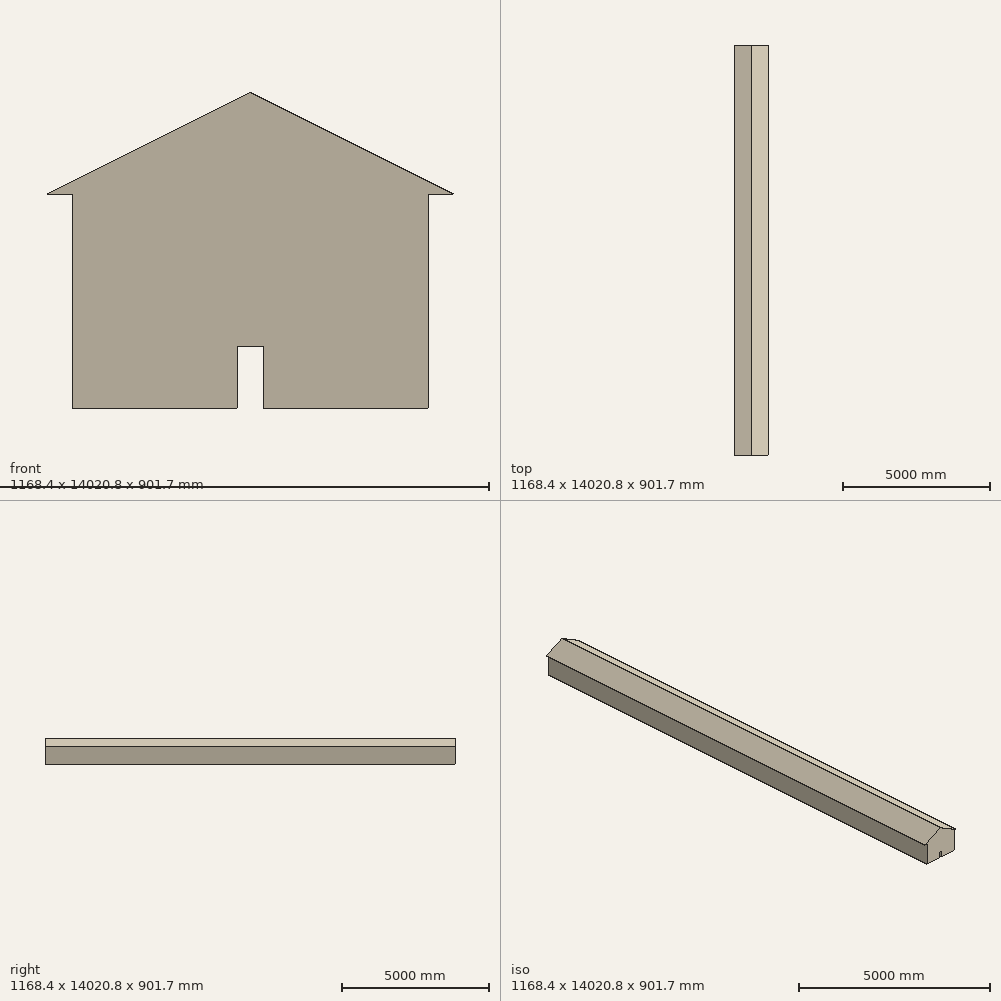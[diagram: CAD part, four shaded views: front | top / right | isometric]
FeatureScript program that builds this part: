
annotation { "Feature Type Name" : "Feature", "Feature Type Description" : "" }
export const myFeature = defineFeature(function(context is Context, id is Id, definition is map)
    precondition{}
    {
        {
            var Q0;
            Q0=qCreatedBy(makeId("Front.planeOp"),FACE);
            var sketch = newSketch(context, id + "F0", { "sketchPlane" : qUnion([Q0])});
            skLineSegment(sketch, "E0", {"start": v(0, 0) * mm, "end": v(-508, 0) * mm});
            skLineSegment(sketch, "E1", {"start": v(0, 0) * mm, "end": v(508, 0) * mm});
            skLineSegment(sketch, "E2", {"start": v(0, 254) * mm, "end": v(0, 0) * mm});
            skLineSegment(sketch, "E3", {"start": v(-508, 0) * mm, "end": v(0, 254) * mm});
            skLineSegment(sketch, "E4", {"start": v(-508, 0) * mm, "end": v(-584.2, 0) * mm});
            skLineSegment(sketch, "E5", {"start": v(508, 0) * mm, "end": v(584.2, 0) * mm});
            skLineSegment(sketch, "E6", {"start": v(0, 254) * mm, "end": v(0, 292.1) * mm});
            skLineSegment(sketch, "E7", {"start": v(-584.2, 0) * mm, "end": v(0, 292.1) * mm});
            skLineSegment(sketch, "E8", {"start": v(-508, 0) * mm, "end": v(-508, -609.6) * mm});
            skLineSegment(sketch, "E9", {"start": v(-508, -609.6) * mm, "end": v(508, -609.6) * mm});
            skLineSegment(sketch, "E10", {"start": v(0, 254) * mm, "end": v(508, 0) * mm});
            skLineSegment(sketch, "E11", {"start": v(0, 292.1) * mm, "end": v(584.2, 0) * mm});
            skLineSegment(sketch, "E12", {"start": v(508, 0) * mm, "end": v(508, -609.6) * mm});
            skLineSegment(sketch, "E13", {"start": v(0, -609.6) * mm, "end": v(-38.1, -609.6) * mm});
            skLineSegment(sketch, "E14", {"start": v(0, -609.6) * mm, "end": v(38.1, -609.6) * mm});
            skLineSegment(sketch, "E15", {"start": v(38.1, -609.6) * mm, "end": v(38.1, -431.8) * mm});
            skLineSegment(sketch, "E16", {"start": v(38.1, -431.8) * mm, "end": v(-38.1, -431.8) * mm});
            skLineSegment(sketch, "E17", {"start": v(-38.1, -431.8) * mm, "end": v(-38.1, -609.6) * mm});
            skLineSegment(sketch, "E18", {"start": v(-508, -609.6) * mm, "end": v(-508, -635) * mm});
            skLineSegment(sketch, "E19", {"start": v(-508, -635) * mm, "end": v(508, -635) * mm});
            skLineSegment(sketch, "E20", {"start": v(508, -635) * mm, "end": v(508, -609.6) * mm});
            skSolve(sketch);
        }
        {
            var Q0;
            Q0=makeQuery(id+"F0.imprint","IMPRINT",FACE,{"disambiguationData":[TD([[makeQuery(id+"F0.imprint","IMPRINT",EDGE,{"derivedFrom":sQuery(id+"F0.wireOp",EDGE,"E0")}),-1.0]])]});
            var Q1;
            Q1=makeQuery(id+"F0.imprint","IMPRINT",FACE,{"disambiguationData":[TD([[makeQuery(id+"F0.imprint","IMPRINT",EDGE,{"derivedFrom":sQuery(id+"F0.wireOp",EDGE,"E3")}),1.0]])]});
            var Q2;
            Q2=makeQuery(id+"F0.imprint","IMPRINT",FACE,{"disambiguationData":[TD([[makeQuery(id+"F0.imprint","IMPRINT",EDGE,{"derivedFrom":sQuery(id+"F0.wireOp",EDGE,"E5")}),1.0]])]});
            var Q3;
            Q3=makeQuery(id+"F0.imprint","IMPRINT",FACE,{"disambiguationData":[TD([[makeQuery(id+"F0.imprint","IMPRINT",EDGE,{"derivedFrom":sQuery(id+"F0.wireOp",EDGE,"E1")}),1.0]])]});
            var Q4;
            Q4=makeQuery(id+"F0.imprint","IMPRINT",FACE,{"disambiguationData":[TD([[makeQuery(id+"F0.imprint","IMPRINT",EDGE,{"derivedFrom":sQuery(id+"F0.wireOp",EDGE,"E0")}),1.0]])]});
            var Q5;
            Q5=makeQuery(id+"F0.imprint","IMPRINT",FACE,{"disambiguationData":[TD([[makeQuery(id+"F0.imprint","IMPRINT",EDGE,{"derivedFrom":sQuery(id+"F0.wireOp",EDGE,"E13")}),-1.0]])]});
            var Q6;
            {var subQ3=sQuery(id+"F0.wireOp",EDGE,"E13");Q6=makeQuery(id+"F0.imprint","IMPRINT",FACE,{"disambiguationData":[TD([[makeQuery(id+"F0.imprint","IMPRINT",EDGE,{"derivedFrom":subQ3}),1.0]])]});}
            extrude(context, id + "F1", {"entities" : qUnion([Q0, Q1, Q2, Q3, Q4, Q5, Q6]), "endBound" : BoundingType.SYMMETRIC, "depth" : 14020.8 * mm, "offsetDistance" : 25.4 * mm});
        }
    });
